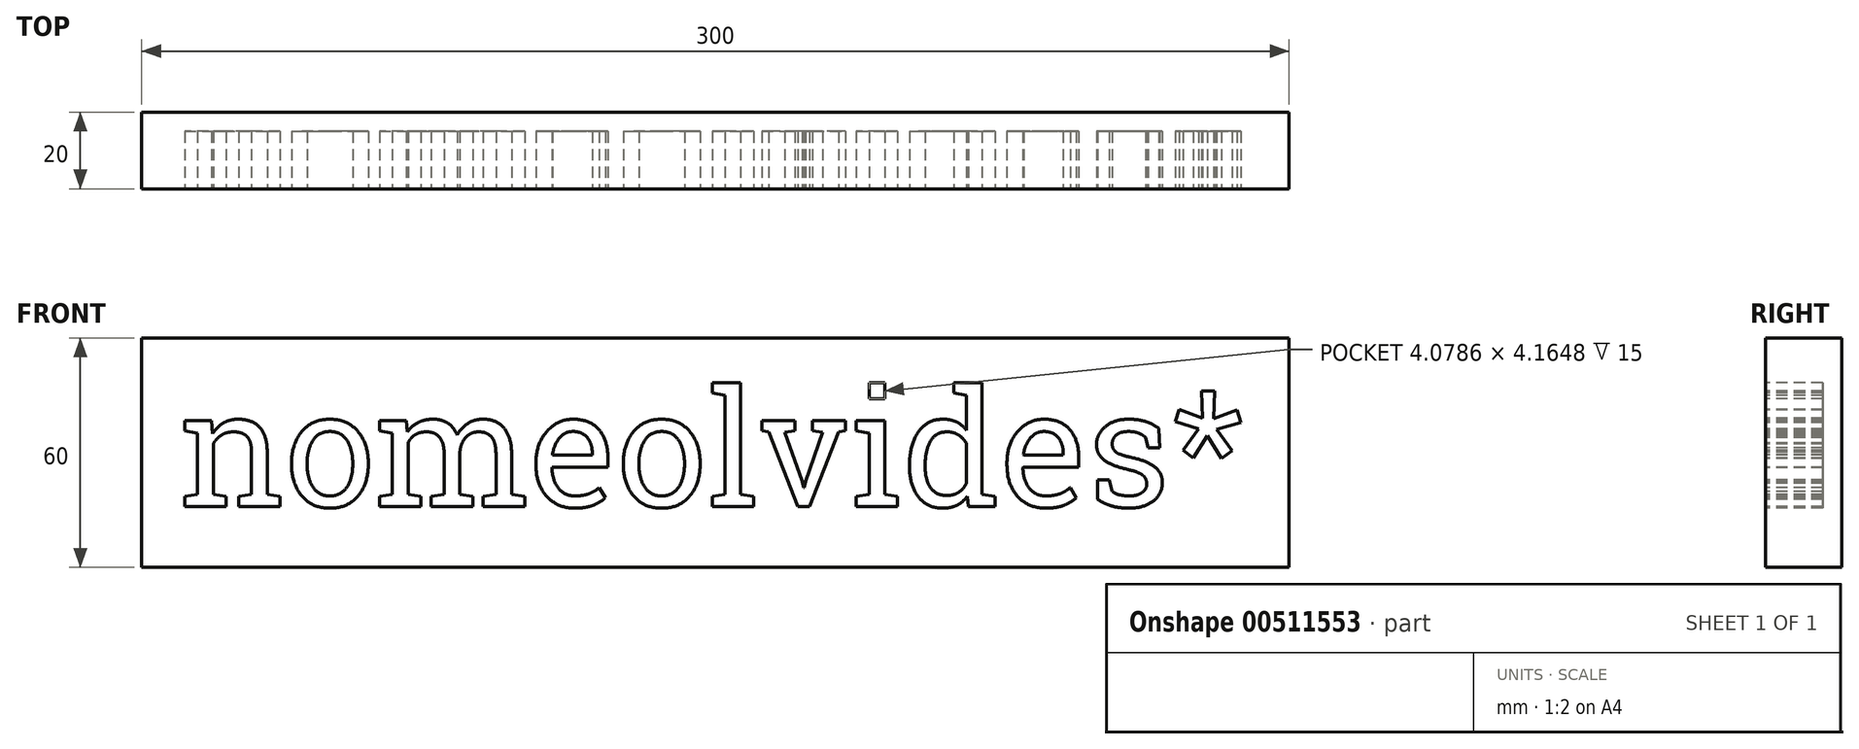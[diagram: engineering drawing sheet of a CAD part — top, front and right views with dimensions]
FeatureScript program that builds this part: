
annotation { "Feature Type Name" : "Feature", "Feature Type Description" : "" }
export const myFeature = defineFeature(function(context is Context, id is Id, definition is map)
    precondition{}
    {
        {
            var Q0;
            Q0=qCreatedBy(makeId("Front.planeOp"),FACE);
            var sketch = newSketch(context, id + "F0", { "sketchPlane" : qUnion([Q0])});
            skLineSegment(sketch, "E0.bottom", {"start": v(-142.2, 60) * mm, "end": v(157.8, 60) * mm});
            skLineSegment(sketch, "E0.top", {"start": v(-142.2, 0) * mm, "end": v(157.8, 0) * mm});
            skLineSegment(sketch, "E0.left", {"start": v(-142.2, 60) * mm, "end": v(-142.2, 0) * mm});
            skLineSegment(sketch, "E0.right", {"start": v(157.8, 60) * mm, "end": v(157.8, 0) * mm});
            skSolve(sketch);
        }
        {
            var Q0;
            Q0=makeQuery(id+"F0.imprint","IMPRINT",FACE,{"disambiguationData":[TD([[makeQuery(id+"F0.imprint","IMPRINT",EDGE,{"derivedFrom":sQuery(id+"F0.wireOp",EDGE,"E0.bottom")}),-1.0]])]});
            extrude(context, id + "F1", {"entities" : qUnion([Q0]), "depth" : 20 * mm});
        }
        {
            var Q0;
            Q0=makeQuery(id+"F1.opExtrude","CAP_FACE",FACE,{"disambiguationData":[OSD([sQuery(id+"F0.wireOp",EDGE,"E0.bottom"),sQuery(id+"F0.wireOp",EDGE,"E0.top"),sQuery(id+"F0.wireOp",EDGE,"E0.left"),sQuery(id+"F0.wireOp",EDGE,"E0.right")])],"isStart":false});
            var sketch = newSketch(context, id + "F2", { "sketchPlane" : qUnion([Q0])});
            skText(sketch, "E1", { "text": "nomeolvides*", "fontName": "RobotoSlab-Regular.ttf"});
            const initialGuessF2  = {"E1": [-0.13219, 0.01589, 1, 0, 0.03056]};
            skSetInitialGuess(sketch, initialGuessF2);
            skSolve(sketch);
        }
        {
            var Q0;
            Q0 = qSketchRegion(id + "F2", true);
            extrude(context, id + "F3", {"entities" : qUnion([Q0]), "operationType" : NewBodyOperationType.REMOVE, "oppositeDirection" : true, "depth" : 15 * mm});
        }
    });
